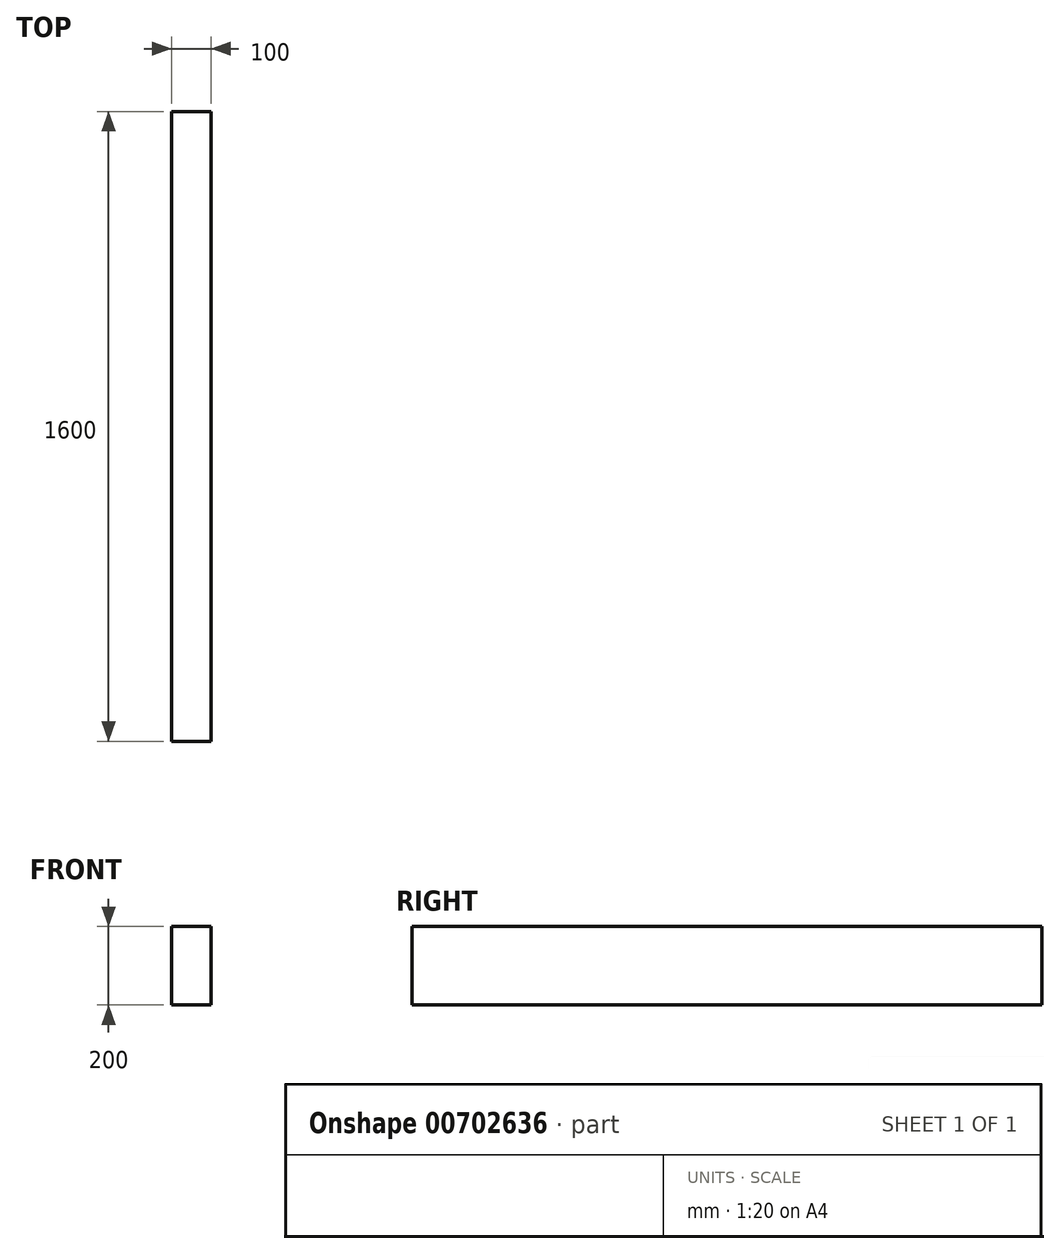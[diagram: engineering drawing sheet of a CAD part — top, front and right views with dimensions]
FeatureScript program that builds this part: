
annotation { "Feature Type Name" : "Feature", "Feature Type Description" : "" }
export const myFeature = defineFeature(function(context is Context, id is Id, definition is map)
    precondition{}
    {
        {
            var Q0;
            Q0=qCreatedBy(makeId("Front.planeOp"),FACE);
            var sketch = newSketch(context, id + "F0", { "sketchPlane" : qUnion([Q0])});
            skLineSegment(sketch, "E0.bottom", {"start": v(0, 0) * mm, "end": v(-100, 0) * mm});
            skLineSegment(sketch, "E0.top", {"start": v(0, 200) * mm, "end": v(-100, 200) * mm});
            skLineSegment(sketch, "E0.left", {"start": v(0, 0) * mm, "end": v(0, 200) * mm});
            skLineSegment(sketch, "E0.right", {"start": v(-100, 0) * mm, "end": v(-100, 200) * mm});
            skSolve(sketch);
        }
        {
            var Q0;
            Q0=qSketchRegion(id+"F0",true);
            extrude(context, id + "F1", {"entities" : qUnion([Q0]), "depth" : 1600 * mm, "offsetDistance" : 25 * mm});
        }
    });
